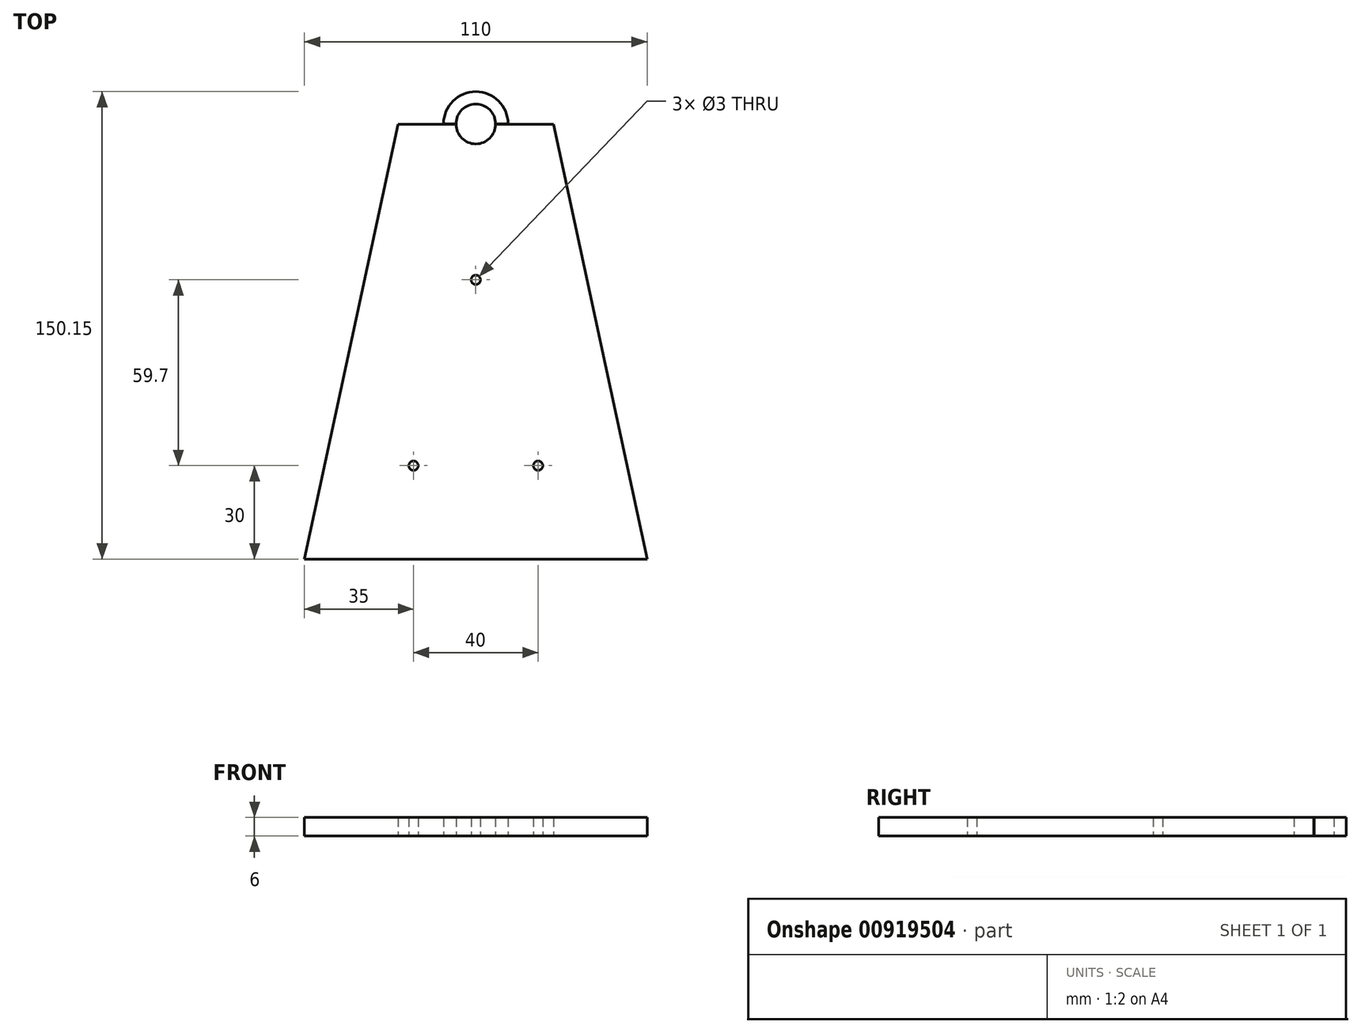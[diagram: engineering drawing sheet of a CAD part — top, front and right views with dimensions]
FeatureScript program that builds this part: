
annotation { "Feature Type Name" : "Feature", "Feature Type Description" : "" }
export const myFeature = defineFeature(function(context is Context, id is Id, definition is map)
    precondition{}
    {
        {
            var Q0;
            Q0=qCreatedBy(makeId("Top.planeOp"),FACE);
            var sketch = newSketch(context, id + "F0", { "sketchPlane" : qUnion([Q0])});
            skLineSegment(sketch, "E0", {"start": v(-20, 0) * mm, "end": v(0, 0) * mm});
            skLineSegment(sketch, "E1", {"start": v(0, 0) * mm, "end": v(20, 0) * mm});
            skCircle(sketch, "E2", {"center": v(-20, 0) * mm, "radius": 1.5 * mm});
            skCircle(sketch, "E3", {"center": v(20, 0) * mm, "radius": 1.5 * mm});
            skLineSegment(sketch, "E4", {"start": v(0, 0) * mm, "end": v(0, -30) * mm});
            skLineSegment(sketch, "E5", {"start": v(0, -30) * mm, "end": v(-55, -30) * mm});
            skLineSegment(sketch, "E6", {"start": v(-55, -30) * mm, "end": v(-25, 109.7) * mm});
            skLineSegment(sketch, "E7", {"start": v(-25, 109.7) * mm, "end": v(25, 109.7) * mm});
            skLineSegment(sketch, "E8", {"start": v(25, 109.7) * mm, "end": v(55, -30) * mm});
            skLineSegment(sketch, "E9", {"start": v(55, -30) * mm, "end": v(0, -30) * mm});
            skLineSegment(sketch, "E10", {"start": v(0, 109.7) * mm, "end": v(0, 59.7) * mm});
            skCircle(sketch, "E11", {"center": v(0, 59.7) * mm, "radius": 1.5 * mm});
            skArc(sketch, "E12", {"start": v(-6.35, 109.7) * mm, "mid": v(0, 103.35) * mm, "end": v(6.35, 109.7) * mm});
            skSolve(sketch);
        }
        {
            var Q0;
            Q0=makeQuery(id+"F0.imprint","IMPRINT",FACE,{"disambiguationData":[TD([[makeQuery(id+"F0.imprint","IMPRINT",EDGE,{"derivedFrom":sQuery(id+"F0.wireOp",EDGE,"E2")}),-1.0]])]});
            extrude(context, id + "F1", {"entities" : qUnion([Q0]), "depth" : 6 * mm, "offsetDistance" : 25 * mm});
        }
        {
            var Q0;
            Q0=makeQuery(id+"F1.opExtrude","CAP_FACE",FACE,{"disambiguationData":[OSD([sQuery(id+"F0.wireOp",EDGE,"E2"),sQuery(id+"F0.wireOp",EDGE,"E3"),sQuery(id+"F0.wireOp",EDGE,"E5"),sQuery(id+"F0.wireOp",EDGE,"E6"),sQuery(id+"F0.wireOp",EDGE,"E7"),sQuery(id+"F0.wireOp",EDGE,"E8"),sQuery(id+"F0.wireOp",EDGE,"E9"),sQuery(id+"F0.wireOp",EDGE,"E11"),sQuery(id+"F0.wireOp",EDGE,"E12")])],"isStart":true});
            var sketch = newSketch(context, id + "F2", { "sketchPlane" : qUnion([Q0])});
            skArc(sketch, "E13", {"start": v(-6.35, -109.8) * mm, "mid": v(0, -116.15) * mm, "end": v(6.35, -109.8) * mm});
            skPoint(sketch, "E14", {"position": v(6.35, -109.8) * mm});
            skPoint(sketch, "E15", {"position": v(-6.35, -109.8) * mm});
            skArc(sketch, "E16", {"start": v(-10.35, -109.8) * mm, "mid": v(0, -120.15) * mm, "end": v(10.35, -109.8) * mm});
            skLineSegment(sketch, "E17", {"start": v(10.35, -109.8) * mm, "end": v(6.35, -109.8) * mm});
            skLineSegment(sketch, "E18", {"start": v(-10.35, -109.8) * mm, "end": v(-6.35, -109.8) * mm});
            skSolve(sketch);
        }
        {
            var Q0;
            Q0=makeQuery(id+"F2.imprint","IMPRINT",FACE,{"disambiguationData":[TD([[makeQuery(id+"F2.imprint","IMPRINT",EDGE,{"derivedFrom":sQuery(id+"F2.wireOp",EDGE,"E13")}),-1.0]])]});
            extrude(context, id + "F3", {"entities" : qUnion([Q0]), "depth" : -6 * mm, "offsetDistance" : 25 * mm});
        }
    });
